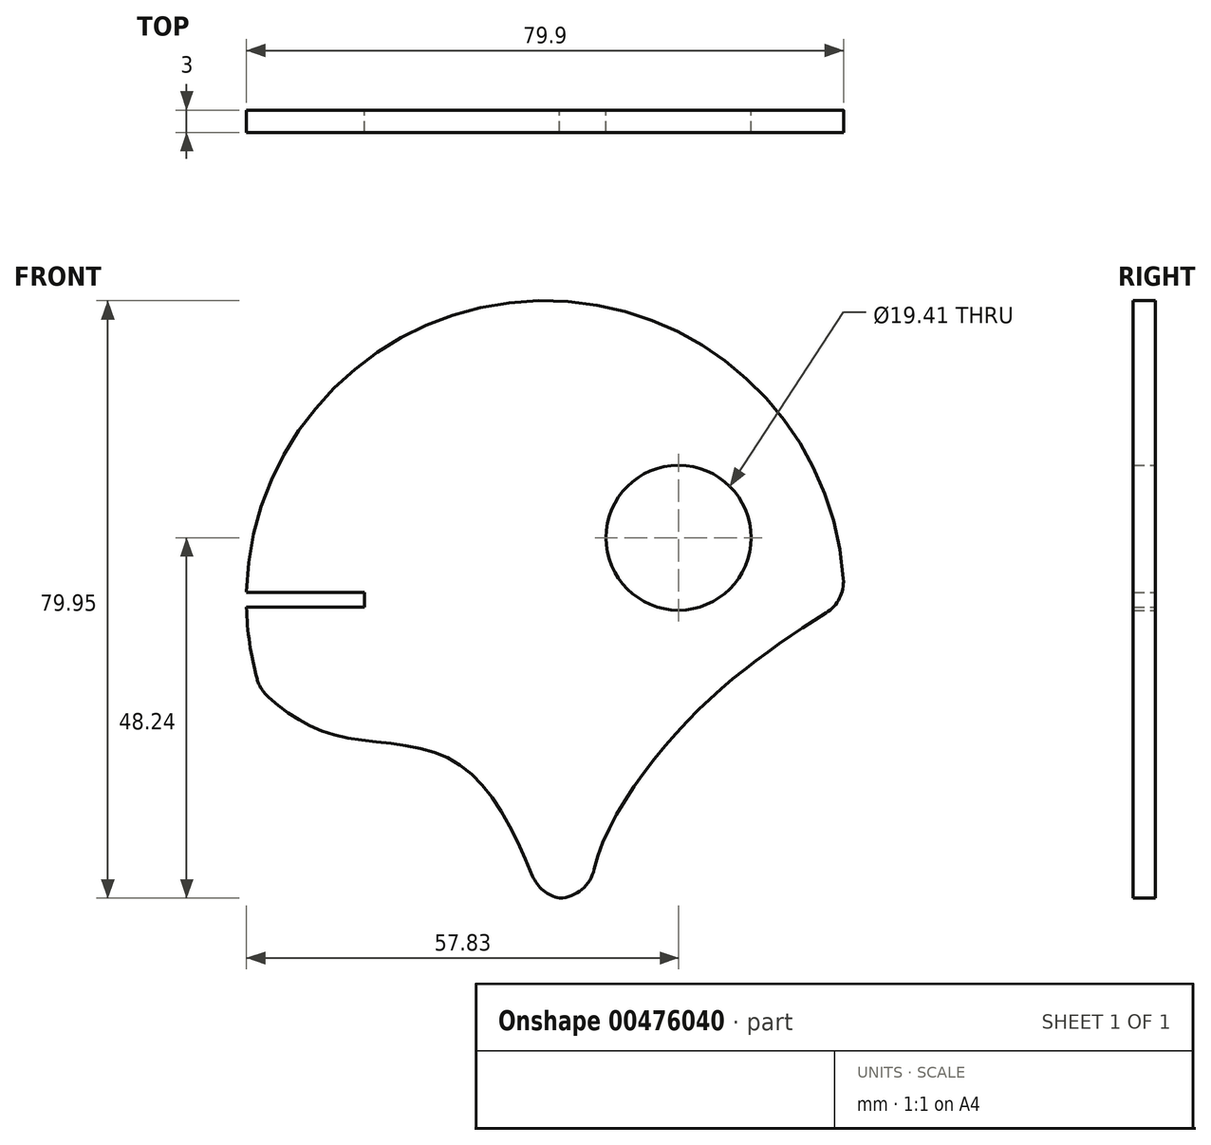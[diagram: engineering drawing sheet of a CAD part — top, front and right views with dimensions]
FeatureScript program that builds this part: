
annotation { "Feature Type Name" : "Feature", "Feature Type Description" : "" }
export const myFeature = defineFeature(function(context is Context, id is Id, definition is map)
    precondition{}
    {
        {
            var Q0;
            Q0=qCreatedBy(makeId("Front.planeOp"),FACE);
            var sketch = newSketch(context, id + "F0", { "sketchPlane" : qUnion([Q0])});
            skCircle(sketch, "E0", {"center": v(0, 0) * mm, "radius": 40 * mm});
            skSolve(sketch);
        }
        {
            var Q0;
            Q0=makeQuery(id+"F0.imprint","IMPRINT",FACE,{"disambiguationData":[TD([[makeQuery(id+"F0.imprint","IMPRINT",EDGE,{"derivedFrom":sQuery(id+"F0.wireOp",EDGE,"E0")}),1.0]])]});
            extrude(context, id + "F1", {"entities" : qUnion([Q0]), "depth" : 3 * mm});
        }
        {
            var Q0;
            Q0=qCreatedBy(makeId("Front.planeOp"),FACE);
            var sketch = newSketch(context, id + "F2", { "sketchPlane" : qUnion([Q0])});
            skLineSegment(sketch, "E1.bottom", {"start": v(-24.17, 1) * mm, "end": v(-57.33, 1) * mm});
            skLineSegment(sketch, "E1.top", {"start": v(-24.17, 0) * mm, "end": v(-57.33, 0) * mm});
            skLineSegment(sketch, "E1.left", {"start": v(-24.17, 1) * mm, "end": v(-24.17, 0) * mm});
            skLineSegment(sketch, "E1.right", {"start": v(-57.33, 1) * mm, "end": v(-57.33, 0) * mm});
            skLineSegment(sketch, "E2.MirrorCS", {"start": v(-24.17, -1) * mm, "end": v(-24.17, 0) * mm});
            skLineSegment(sketch, "E3.MirrorCS", {"start": v(-24.17, -1) * mm, "end": v(-57.33, -1) * mm});
            skLineSegment(sketch, "E4.MirrorCS", {"start": v(-57.33, -1) * mm, "end": v(-57.33, 0) * mm});
            skSolve(sketch);
        }
        {
            var Q0;
            Q0=makeQuery(id+"F2.imprint","IMPRINT",FACE,{"disambiguationData":[TD([[makeQuery(id+"F2.imprint","IMPRINT",EDGE,{"derivedFrom":sQuery(id+"F2.wireOp",EDGE,"E1.bottom")}),1.0]])]});
            extrude(context, id + "F3", {"entities" : qUnion([Q0]), "operationType" : NewBodyOperationType.REMOVE, "depth" : 24.9 * mm});
        }
        {
            var Q0;
            Q0 = qSketchRegion(id + "F2", true);
            extrude(context, id + "F4", {"entities" : qUnion([Q0]), "operationType" : NewBodyOperationType.REMOVE, "depth" : 25 * mm});
        }
        {
            var Q0;
            Q0=qCreatedBy(makeId("Front.planeOp"),FACE);
            var sketch = newSketch(context, id + "F5", { "sketchPlane" : qUnion([Q0])});
            skCircle(sketch, "E5", {"center": v(17.84, 8.29) * mm, "radius": 9.7 * mm});
            skSolve(sketch);
        }
        {
            var Q0;
            Q0 = qSketchRegion(id + "F5", true);
            extrude(context, id + "F6", {"entities" : qUnion([Q0]), "operationType" : NewBodyOperationType.REMOVE, "depth" : 25 * mm, "offsetDistance" : 25 * mm});
        }
        {
            var Q0;
            Q0=qCreatedBy(makeId("Front.planeOp"),FACE);
            var sketch = newSketch(context, id + "F7", { "sketchPlane" : qUnion([Q0])});
            skFitSpline(sketch, "E6", {"points": [v(40.43, 0) * mm, v(17.72, -17.66) * mm, v(6.9, -42.17) * mm, v(45.83, -50.1) * mm], "startDerivative": vector(-72.58, -45.36) * mm, "endDerivative": vector(141.89, -2.43) * mm});
            skLineSegment(sketch, "E7", {"start": v(40.43, 0) * mm, "end": v(45.83, -50.1) * mm});
            skFitSpline(sketch, "E8", {"points": [v(32.72, -4.81) * mm, v(52.32, 17.66) * mm, v(52.68, 39.28) * mm, v(60.25, 34.24) * mm], "startDerivative": vector(63.3, 44.69) * mm, "endDerivative": vector(41.93, -39.85) * mm});
            skLineSegment(sketch, "E9", {"start": v(60.25, 34.24) * mm, "end": v(41.5, 1.38) * mm});
            skLineSegment(sketch, "E10", {"start": v(41.5, 1.38) * mm, "end": v(40.43, 0) * mm});
            skSolve(sketch);
        }
        {
            var Q0;
            Q0 = qSketchRegion(id + "F7", true);
            extrude(context, id + "F8", {"entities" : qUnion([Q0]), "operationType" : NewBodyOperationType.REMOVE, "depth" : 25 * mm, "offsetDistance" : 25 * mm});
        }
        {
            var Q0;
            Q0=makeQuery(id+"F8.boolean.opBoolean","INTERSECT",EDGE,{"disambiguationData":[OD(0.0)],"derivedFrom":[makeQuery(id+"F1.opExtrude","SWEPT_FACE",FACE,{"disambiguationData":[OSD([sQuery(id+"F0.wireOp",EDGE,"E0")])]}),makeQuery(id+"F8.opExtrude","SWEPT_FACE",FACE,{"disambiguationData":[OSD([sQuery(id+"F7.wireOp",EDGE,"E6")])]})]});
            fillet(context, id + "F9", {"entities" : qUnion([Q0]), "radius" : 5 * mm, "tangentPropagation" : true, "allowEdgeOverflow" : false});
        }
        {
            var Q0;
            Q0=makeQuery(id+"F8.boolean.opBoolean","INTERSECT",EDGE,{"disambiguationData":[OD(1.0)],"derivedFrom":[makeQuery(id+"F1.opExtrude","SWEPT_FACE",FACE,{"disambiguationData":[OSD([sQuery(id+"F0.wireOp",EDGE,"E0")])]}),makeQuery(id+"F8.opExtrude","SWEPT_FACE",FACE,{"disambiguationData":[OSD([sQuery(id+"F7.wireOp",EDGE,"E6")])]})]});
            fillet(context, id + "F10", {"entities" : qUnion([Q0]), "radius" : 5 * mm, "tangentPropagation" : true, "allowEdgeOverflow" : false});
        }
        {
            var Q0;
            Q0=qCreatedBy(makeId("Front.planeOp"),FACE);
            var sketch = newSketch(context, id + "F11", { "sketchPlane" : qUnion([Q0])});
            skFitSpline(sketch, "E11", {"points": [v(0, -41.13) * mm, v(-12.19, -21.63) * mm, v(-28.69, -17.98) * mm, v(-39.4, -10.91) * mm], "startDerivative": vector(-25.48, 63.23) * mm, "endDerivative": vector(-33.12, 30.3) * mm});
            skLineSegment(sketch, "E12", {"start": v(-39.4, -10.91) * mm, "end": v(-30.19, -40.27) * mm});
            skLineSegment(sketch, "E13", {"start": v(-30.19, -40.27) * mm, "end": v(0, -41.13) * mm});
            skSolve(sketch);
        }
        {
            var Q0;
            Q0 = qSketchRegion(id + "F11", true);
            extrude(context, id + "F12", {"entities" : qUnion([Q0]), "operationType" : NewBodyOperationType.REMOVE, "depth" : 25 * mm, "offsetDistance" : 25 * mm});
        }
        {
            var Q0;
            {var subQ0=sQuery(id+"F0.wireOp",EDGE,"E0");Q0=makeQuery(id+"F12.boolean.opBoolean","INTERSECT",EDGE,{"disambiguationData":[OD(0.0)],"derivedFrom":[makeQuery(id+"F8.boolean.opBoolean","SPLIT",FACE,{"disambiguationData":[TD([makeQuery(id+"F4.boolean.opBoolean","COPY",FACE,{"derivedFrom":makeQuery(id+"F4.opExtrude","SWEPT_FACE",FACE,{"disambiguationData":[OSD([sQuery(id+"F2.wireOp",EDGE,"E3.MirrorCS")])]})})])],"derivedFrom":makeQuery(id+"F1.opExtrude","SWEPT_FACE",FACE,{"disambiguationData":[OSD([subQ0])]})}),makeQuery(id+"F12.opExtrude","SWEPT_FACE",FACE,{"disambiguationData":[OSD([sQuery(id+"F11.wireOp",EDGE,"E11")])]})]});}
            fillet(context, id + "F13", {"entities" : qUnion([Q0]), "radius" : 5 * mm, "tangentPropagation" : true, "allowEdgeOverflow" : false});
        }
        {
            var Q0;
            {var subQ0=sQuery(id+"F0.wireOp",EDGE,"E0");Q0=makeQuery(id+"F12.boolean.opBoolean","INTERSECT",EDGE,{"disambiguationData":[OD(1.0)],"derivedFrom":[makeQuery(id+"F8.boolean.opBoolean","SPLIT",FACE,{"disambiguationData":[TD([makeQuery(id+"F4.boolean.opBoolean","COPY",FACE,{"derivedFrom":makeQuery(id+"F4.opExtrude","SWEPT_FACE",FACE,{"disambiguationData":[OSD([sQuery(id+"F2.wireOp",EDGE,"E3.MirrorCS")])]})})])],"derivedFrom":makeQuery(id+"F1.opExtrude","SWEPT_FACE",FACE,{"disambiguationData":[OSD([subQ0])]})}),makeQuery(id+"F12.opExtrude","SWEPT_FACE",FACE,{"disambiguationData":[OSD([sQuery(id+"F11.wireOp",EDGE,"E11")])]})]});}
            fillet(context, id + "F14", {"entities" : qUnion([Q0]), "radius" : 5 * mm, "tangentPropagation" : true, "allowEdgeOverflow" : false});
        }
    });
